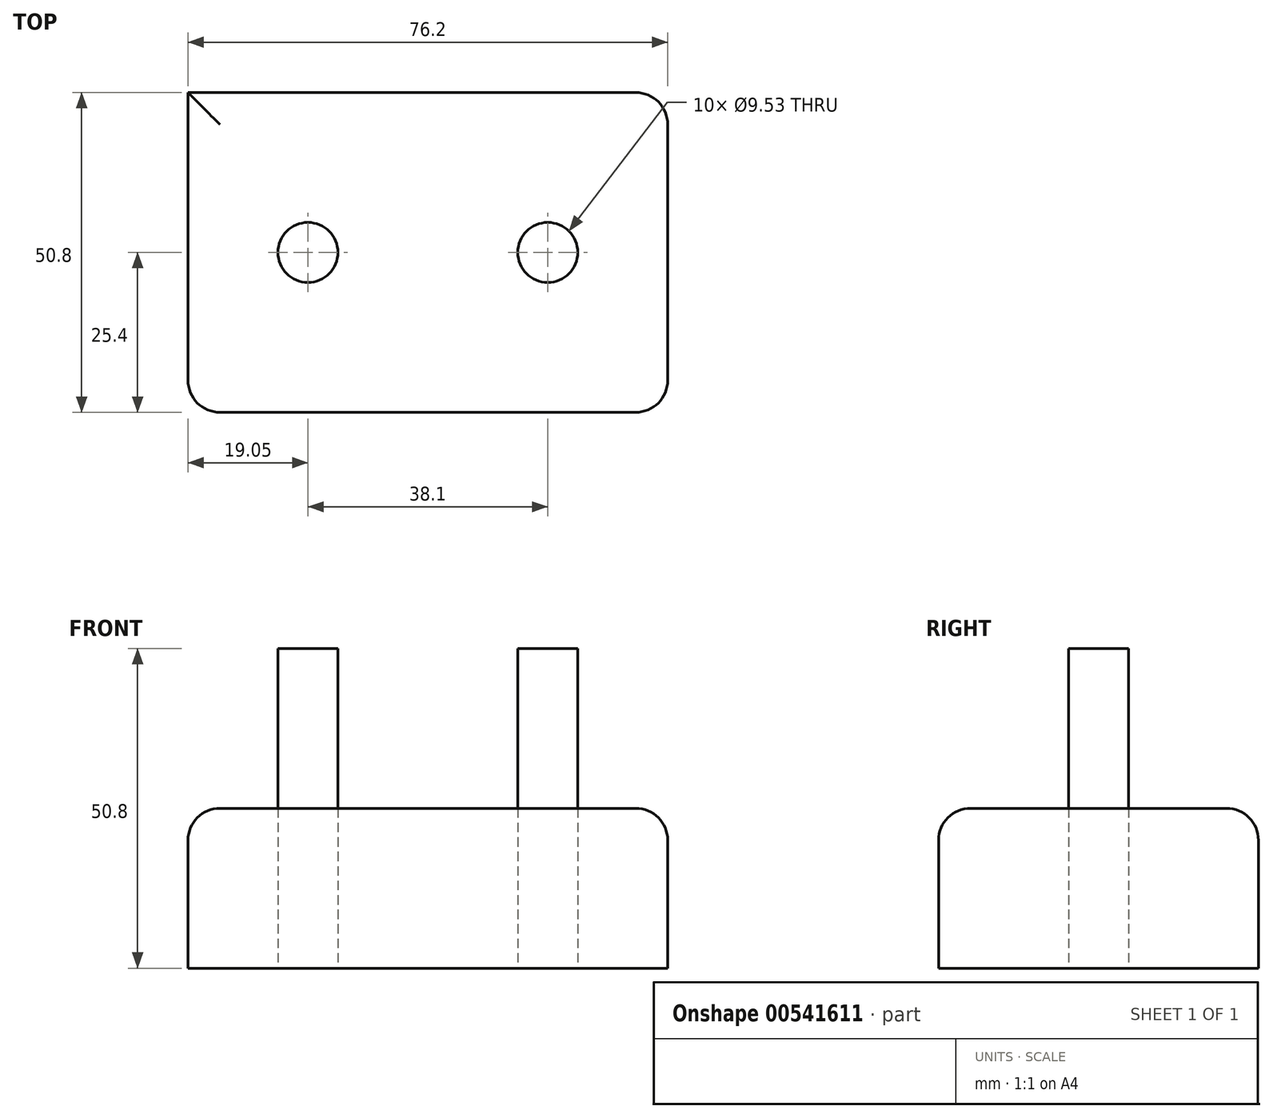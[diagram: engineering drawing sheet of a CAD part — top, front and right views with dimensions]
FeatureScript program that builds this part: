
annotation { "Feature Type Name" : "Feature", "Feature Type Description" : "" }
export const myFeature = defineFeature(function(context is Context, id is Id, definition is map)
    precondition{}
    {
        {
            var Q0;
            Q0=qCreatedBy(makeId("Top.planeOp"),FACE);
            var sketch = newSketch(context, id + "F0", { "sketchPlane" : qUnion([Q0])});
            skLineSegment(sketch, "E0.bottom", {"start": v(38.1, 25.4) * mm, "end": v(-38.1, 25.4) * mm});
            skLineSegment(sketch, "E0.top", {"start": v(38.1, -25.4) * mm, "end": v(-38.1, -25.4) * mm});
            skLineSegment(sketch, "E0.left", {"start": v(38.1, 25.4) * mm, "end": v(38.1, -25.4) * mm});
            skLineSegment(sketch, "E0.right", {"start": v(-38.1, 25.4) * mm, "end": v(-38.1, -25.4) * mm});
            skPoint(sketch, "E0.middle", {"position": v(0, 0) * mm});
            skCircle(sketch, "E1", {"center": v(-19.05, 0) * mm, "radius": 4.76 * mm});
            skCircle(sketch, "E2", {"center": v(19.05, 0) * mm, "radius": 4.76 * mm});
            skSolve(sketch);
        }
        {
            var Q0;
            Q0=makeQuery(id+"F0.imprint","IMPRINT",FACE,{"disambiguationData":[TD([[makeQuery(id+"F0.imprint","IMPRINT",EDGE,{"derivedFrom":sQuery(id+"F0.wireOp",EDGE,"E0.bottom")}),1.0]])]});
            extrude(context, id + "F1", {"entities" : qUnion([Q0]), "depth" : 25.4 * mm, "offsetDistance" : 25.4 * mm});
        }
        {
            var Q0;
            Q0=makeQuery(id+"F0.imprint","IMPRINT",FACE,{"disambiguationData":[TD([[makeQuery(id+"F0.imprint","IMPRINT",EDGE,{"derivedFrom":sQuery(id+"F0.wireOp",EDGE,"E1")}),1.0]])]});
            var Q1;
            Q1=makeQuery(id+"F0.imprint","IMPRINT",FACE,{"disambiguationData":[TD([[makeQuery(id+"F0.imprint","IMPRINT",EDGE,{"derivedFrom":sQuery(id+"F0.wireOp",EDGE,"E2")}),1.0]])]});
            extrude(context, id + "F2", {"entities" : qUnion([Q0, Q1]), "depth" : 50.8 * mm, "offsetDistance" : 25.4 * mm});
        }
        {
            var Q0;
            Q0=makeQuery(id+"F1.opExtrude","CAP_EDGE",EDGE,{"disambiguationData":[OSD([sQuery(id+"F0.wireOp",EDGE,"E0.top")])],"isStart":false});
            var Q1;
            Q1=makeQuery(id+"F1.opExtrude","CAP_EDGE",EDGE,{"disambiguationData":[OSD([sQuery(id+"F0.wireOp",EDGE,"E0.right")])],"isStart":false});
            var Q2;
            Q2=makeQuery(id+"F1.opExtrude","CAP_EDGE",EDGE,{"disambiguationData":[OSD([sQuery(id+"F0.wireOp",EDGE,"E0.bottom")])],"isStart":false});
            var Q3;
            Q3=makeQuery(id+"F1.opExtrude","CAP_EDGE",EDGE,{"disambiguationData":[OSD([sQuery(id+"F0.wireOp",EDGE,"E0.left")])],"isStart":false});
            var Q4;
            Q4=makeQuery(id+"F1.opExtrude","SWEPT_EDGE",EDGE,{"disambiguationData":[OSD([sQuery(id+"F0.wireOp",EDGE,"E0.top"),sQuery(id+"F0.wireOp",EDGE,"E0.left")])]});
            var Q5;
            Q5=makeQuery(id+"F1.opExtrude","SWEPT_EDGE",EDGE,{"disambiguationData":[OSD([sQuery(id+"F0.wireOp",EDGE,"E0.top"),sQuery(id+"F0.wireOp",EDGE,"E0.right")])]});
            var Q6;
            Q6=makeQuery(id+"F1.opExtrude","SWEPT_EDGE",EDGE,{"disambiguationData":[OSD([sQuery(id+"F0.wireOp",EDGE,"E0.bottom"),sQuery(id+"F0.wireOp",EDGE,"E0.left")])]});
            fillet(context, id + "F3", {"entities" : qUnion([Q0, Q1, Q2, Q3, Q4, Q5, Q6]), "radius" : 5.08 * mm, "tangentPropagation" : true, "allowEdgeOverflow" : false});
        }
    });
